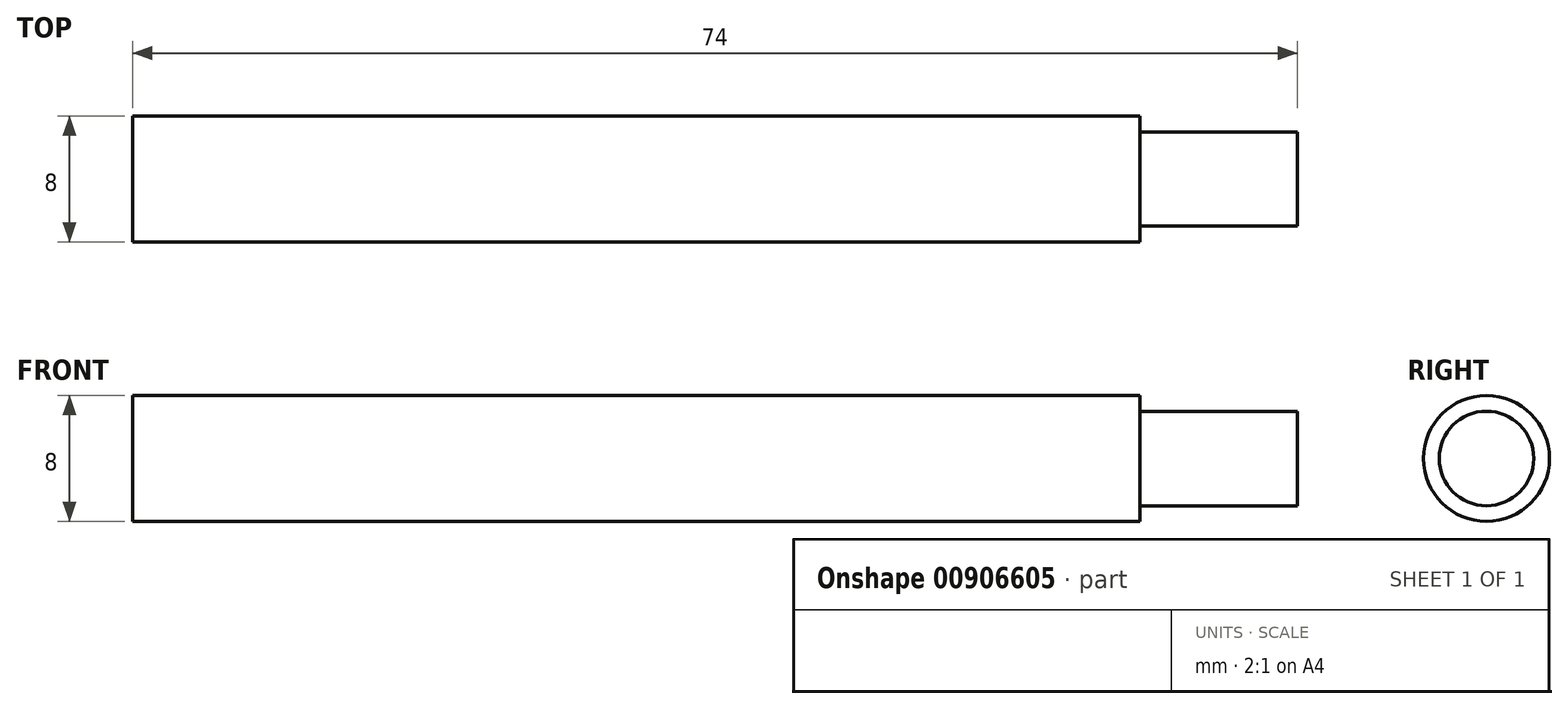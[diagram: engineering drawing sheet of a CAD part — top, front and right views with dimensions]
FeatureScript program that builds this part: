
annotation { "Feature Type Name" : "Feature", "Feature Type Description" : "" }
export const myFeature = defineFeature(function(context is Context, id is Id, definition is map)
    precondition{}
    {
        {
            var Q0;
            Q0=qCreatedBy(makeId("Front.planeOp"),FACE);
            var sketch = newSketch(context, id + "F0", { "sketchPlane" : qUnion([Q0])});
            skLineSegment(sketch, "E0", {"start": v(0, 0) * mm, "end": v(0, 4) * mm});
            skLineSegment(sketch, "E1", {"start": v(0, 4) * mm, "end": v(64, 4) * mm});
            skLineSegment(sketch, "E2", {"start": v(64, 4) * mm, "end": v(64, 3) * mm});
            skLineSegment(sketch, "E3", {"start": v(64, 3) * mm, "end": v(74, 3) * mm});
            skLineSegment(sketch, "E4", {"start": v(74, 3) * mm, "end": v(74, 0) * mm});
            skLineSegment(sketch, "E5", {"start": v(74, 0) * mm, "end": v(0, 0) * mm});
            skSolve(sketch);
        }
        {
            var Q0;
            Q0 = qSketchRegion(id + "F0", true);
            var Q1;
            Q1=sQuery(id+"F0.wireOp",EDGE,"E5");
            revolve(context, id + "F1", {"surfaceOperationType" : NewSurfaceOperationType.NEW, "entities" : qUnion([Q0]), "axis" : qUnion([Q1]), "revolveType" : RevolveType.FULL});
        }
    });
